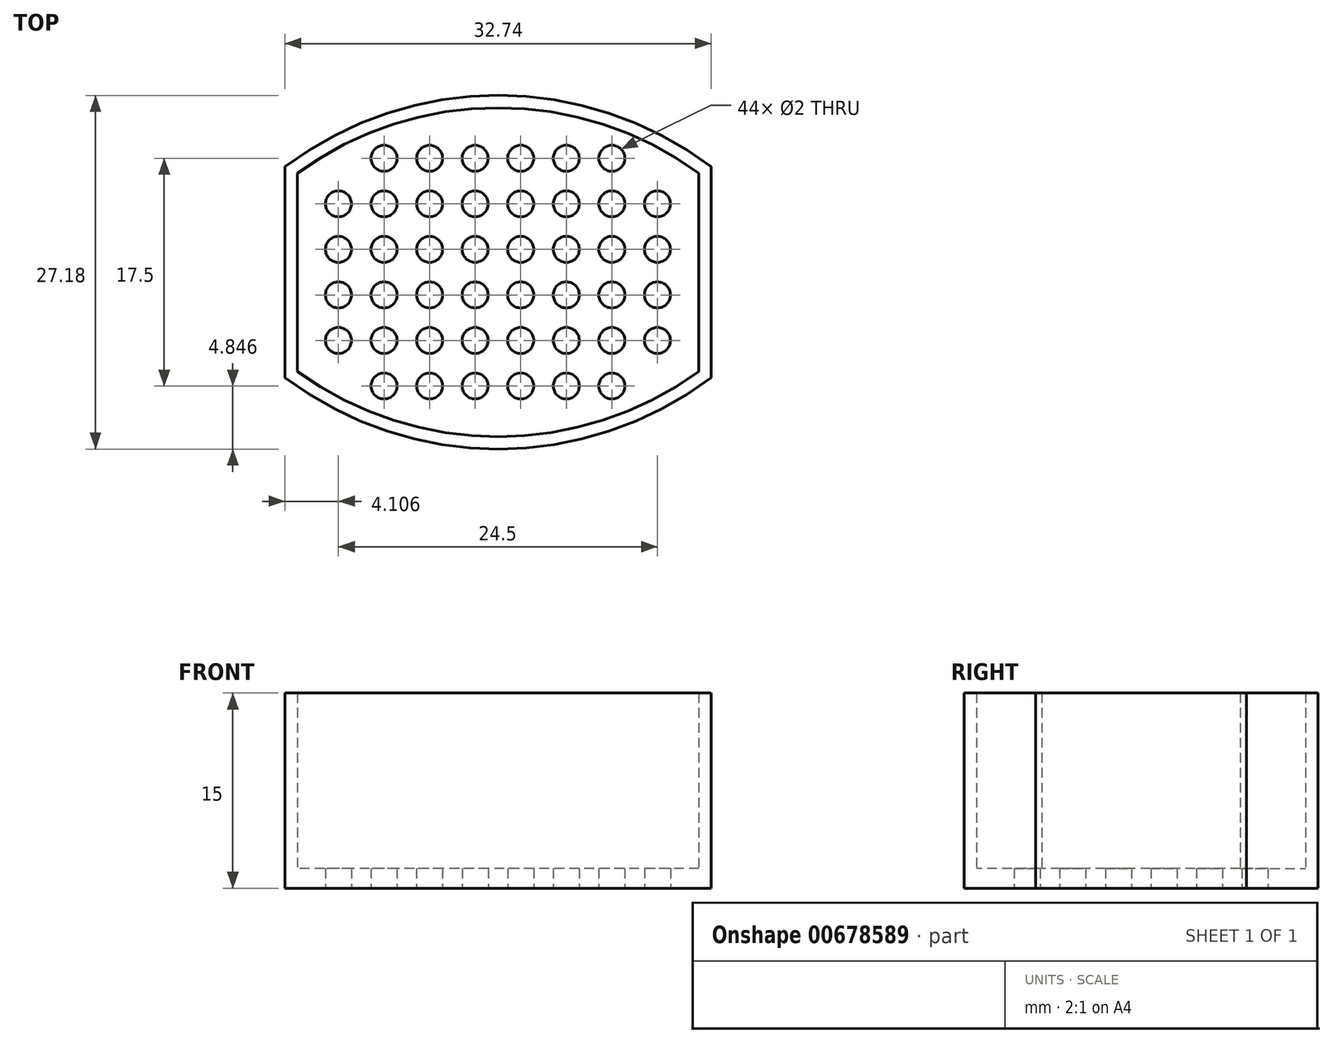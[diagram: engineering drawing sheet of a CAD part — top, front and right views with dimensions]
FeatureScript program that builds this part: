
annotation { "Feature Type Name" : "Feature", "Feature Type Description" : "" }
export const myFeature = defineFeature(function(context is Context, id is Id, definition is map)
    precondition{}
    {
        {
            var Q0;
            Q0=qCreatedBy(makeId("Top.planeOp"),FACE);
            var sketch = newSketch(context, id + "F0", { "sketchPlane" : qUnion([Q0])});
            skArc(sketch, "E0.0", {"start": v(-13.39, -2.84) * mm, "mid": v(-29.76, 2.65) * mm, "end": v(-46.13, -2.84) * mm});
            skLineSegment(sketch, "E0.1", {"start": v(-13.39, -2.84) * mm, "end": v(-13.39, -19.04) * mm});
            skArc(sketch, "E0.2", {"start": v(-46.13, -19.04) * mm, "mid": v(-29.76, -24.53) * mm, "end": v(-13.39, -19.04) * mm});
            skLineSegment(sketch, "E0.3", {"start": v(-46.13, -2.84) * mm, "end": v(-46.13, -19.04) * mm});
            skArc(sketch, "E1.0", {"start": v(-14.34, -3.32) * mm, "mid": v(-29.76, 1.7) * mm, "end": v(-45.17, -3.32) * mm});
            skLineSegment(sketch, "E1.1", {"start": v(-14.34, -3.32) * mm, "end": v(-14.34, -18.56) * mm});
            skArc(sketch, "E1.2", {"start": v(-45.17, -18.56) * mm, "mid": v(-29.76, -23.58) * mm, "end": v(-14.34, -18.56) * mm});
            skLineSegment(sketch, "E1.3", {"start": v(-45.17, -3.32) * mm, "end": v(-45.17, -18.56) * mm});
            skCircle(sketch, "E2", {"center": v(-28.02, -12.68) * mm, "radius": 1 * mm});
            skCircle(sketch, "E3", {"center": v(-28.02, -16.18) * mm, "radius": 1 * mm});
            skCircle(sketch, "E4", {"center": v(-28.02, -19.68) * mm, "radius": 1 * mm});
            skCircle(sketch, "E5", {"center": v(-24.52, -12.68) * mm, "radius": 1 * mm});
            skCircle(sketch, "E6", {"center": v(-24.52, -16.18) * mm, "radius": 1 * mm});
            skCircle(sketch, "E7", {"center": v(-24.52, -19.68) * mm, "radius": 1 * mm});
            skCircle(sketch, "E8", {"center": v(-21.02, -12.68) * mm, "radius": 1 * mm});
            skCircle(sketch, "E9", {"center": v(-21.02, -16.18) * mm, "radius": 1 * mm});
            skCircle(sketch, "E10", {"center": v(-35.02, -12.68) * mm, "radius": 1 * mm});
            skCircle(sketch, "E11", {"center": v(-35.02, -16.18) * mm, "radius": 1 * mm});
            skCircle(sketch, "E12", {"center": v(-35.02, -19.68) * mm, "radius": 1 * mm});
            skCircle(sketch, "E13", {"center": v(-31.52, -12.68) * mm, "radius": 1 * mm});
            skCircle(sketch, "E14", {"center": v(-31.52, -16.18) * mm, "radius": 1 * mm});
            skCircle(sketch, "E15", {"center": v(-31.52, -19.68) * mm, "radius": 1 * mm});
            skCircle(sketch, "E16", {"center": v(-17.52, -12.68) * mm, "radius": 1 * mm});
            skCircle(sketch, "E17", {"center": v(-17.52, -16.18) * mm, "radius": 1 * mm});
            skCircle(sketch, "E18", {"center": v(-42.02, -12.68) * mm, "radius": 1 * mm});
            skCircle(sketch, "E19", {"center": v(-42.02, -16.18) * mm, "radius": 1 * mm});
            skCircle(sketch, "E20", {"center": v(-38.52, -12.68) * mm, "radius": 1 * mm});
            skCircle(sketch, "E21", {"center": v(-38.52, -16.18) * mm, "radius": 1 * mm});
            skCircle(sketch, "E22", {"center": v(-38.52, -19.68) * mm, "radius": 1 * mm});
            skCircle(sketch, "E23", {"center": v(-21.02, -19.68) * mm, "radius": 1 * mm});
            skCircle(sketch, "E24", {"center": v(-28.02, -9.18) * mm, "radius": 1 * mm});
            skCircle(sketch, "E25", {"center": v(-24.52, -9.18) * mm, "radius": 1 * mm});
            skCircle(sketch, "E26", {"center": v(-21.02, -9.18) * mm, "radius": 1 * mm});
            skCircle(sketch, "E27", {"center": v(-35.02, -9.18) * mm, "radius": 1 * mm});
            skCircle(sketch, "E28", {"center": v(-31.52, -9.18) * mm, "radius": 1 * mm});
            skCircle(sketch, "E29", {"center": v(-17.52, -9.18) * mm, "radius": 1 * mm});
            skCircle(sketch, "E30", {"center": v(-42.02, -9.18) * mm, "radius": 1 * mm});
            skCircle(sketch, "E31", {"center": v(-38.52, -9.18) * mm, "radius": 1 * mm});
            skCircle(sketch, "E32", {"center": v(-28.02, -5.68) * mm, "radius": 1 * mm});
            skCircle(sketch, "E33", {"center": v(-24.52, -5.68) * mm, "radius": 1 * mm});
            skCircle(sketch, "E34", {"center": v(-21.02, -5.68) * mm, "radius": 1 * mm});
            skCircle(sketch, "E35", {"center": v(-35.02, -5.68) * mm, "radius": 1 * mm});
            skCircle(sketch, "E36", {"center": v(-31.52, -5.68) * mm, "radius": 1 * mm});
            skCircle(sketch, "E37", {"center": v(-17.52, -5.68) * mm, "radius": 1 * mm});
            skCircle(sketch, "E38", {"center": v(-42.02, -5.68) * mm, "radius": 1 * mm});
            skCircle(sketch, "E39", {"center": v(-38.52, -5.68) * mm, "radius": 1 * mm});
            skCircle(sketch, "E40", {"center": v(-28.02, -2.18) * mm, "radius": 1 * mm});
            skCircle(sketch, "E41", {"center": v(-24.52, -2.18) * mm, "radius": 1 * mm});
            skCircle(sketch, "E42", {"center": v(-21.02, -2.18) * mm, "radius": 1 * mm});
            skCircle(sketch, "E43", {"center": v(-35.02, -2.18) * mm, "radius": 1 * mm});
            skCircle(sketch, "E44", {"center": v(-31.52, -2.18) * mm, "radius": 1 * mm});
            skCircle(sketch, "E45", {"center": v(-38.52, -2.18) * mm, "radius": 1 * mm});
            skSolve(sketch);
        }
        {
            var Q0;
            Q0=makeQuery(id+"F0.imprint","IMPRINT",FACE,{"disambiguationData":[TD([[makeQuery(id+"F0.imprint","IMPRINT",EDGE,{"derivedFrom":sQuery(id+"F0.wireOp",EDGE,"E0.0")}),1.0]])]});
            extrude(context, id + "F1", {"entities" : qUnion([Q0]), "depth" : 15 * mm, "offsetDistance" : 25 * mm});
        }
        {
            var Q0;
            Q0=makeQuery(id+"F0.imprint","IMPRINT",FACE,{"disambiguationData":[TD([[makeQuery(id+"F0.imprint","IMPRINT",EDGE,{"derivedFrom":sQuery(id+"F0.wireOp",EDGE,"E1.0")}),1.0]])]});
            extrude(context, id + "F2", {"entities" : qUnion([Q0]), "operationType" : NewBodyOperationType.ADD, "depth" : 1.5 * mm, "offsetDistance" : 25 * mm});
        }
    });
